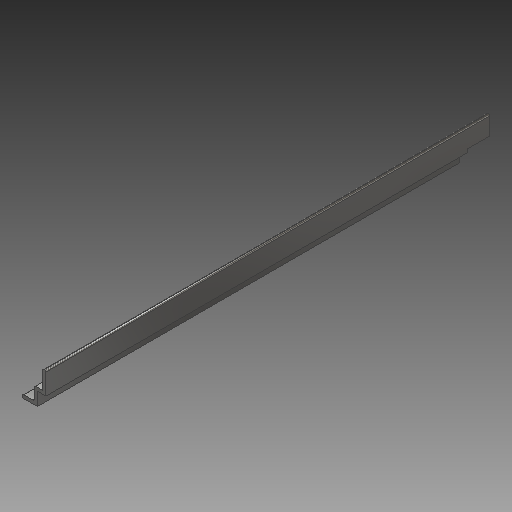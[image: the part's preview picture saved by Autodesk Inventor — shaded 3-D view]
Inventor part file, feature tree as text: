
AUTODESK INVENTOR PART (.ipt)
format: ipt  version: 2019 (Build 230136000, 136)  size: 154,112 bytes
history: native  units: mm
features: extrude x2, fillet x2, sketch x2
ambient origin geometry x8: Origin, YZ Plane, XZ Plane, XY Plane, X Axis, Y Axis, Z Axis, Center Point
bodies: Body1 (feature_tree)
feature tree (6):
  extrude  "Extrusion2"  Depth=48.0mm
  fillet  "Fillet2"  Radius=30.0mm
  extrude  "Extrusion4"  Depth=11.5mm
  fillet  "Fillet3"  Radius=16.0mm
  sketch  "Sketch1"  dims[d0=20.5mm d1=48.0mm d9=30.0mm]
  sketch  "Sketch9"  dims[d10=32.0mm d11=11.5mm d16=16.0mm d20=600.0mm d21=0.0mm d23=4.5mm d24=4.5mm d25=4.5mm d26=2.0mm d86=50.0mm d87=0.0mm d88=30.0mm d89=2.0mm]
